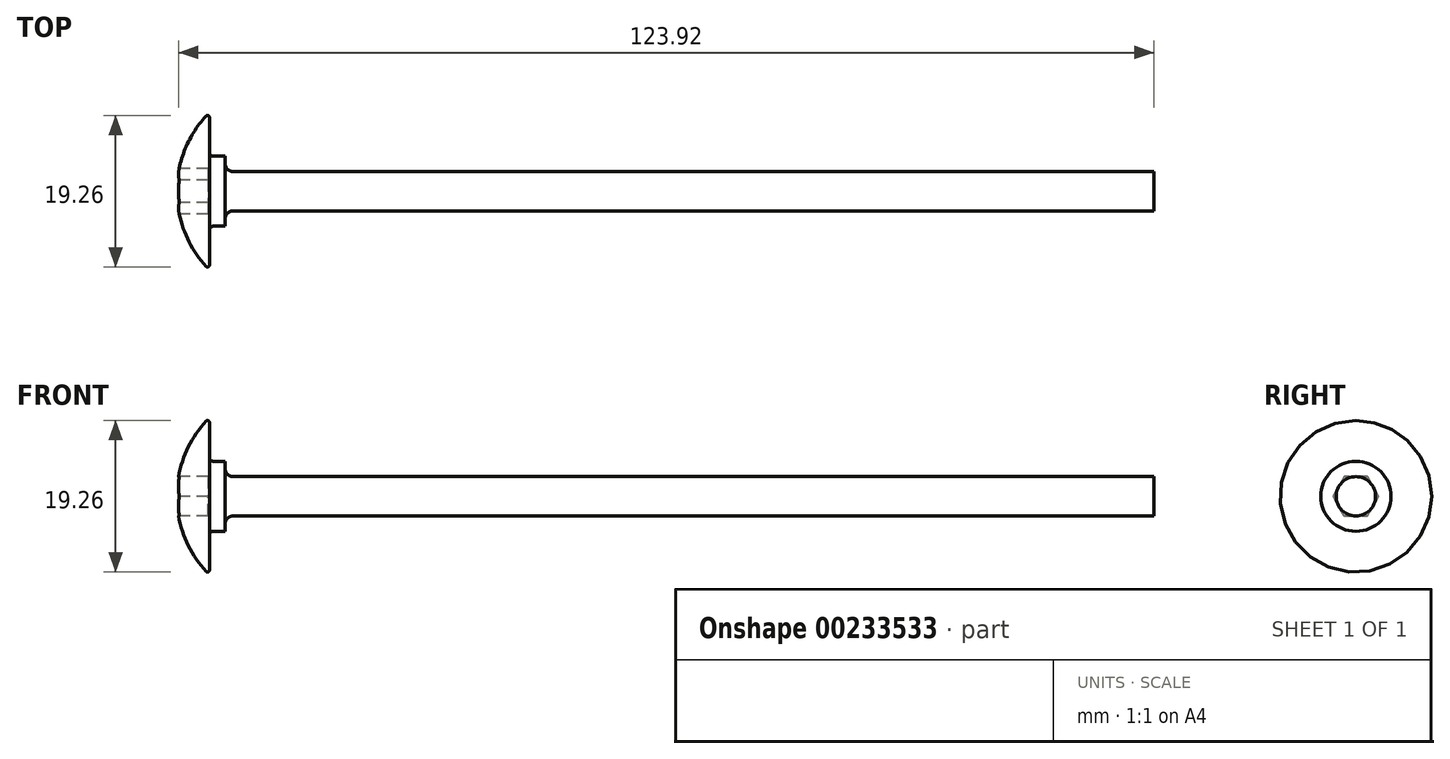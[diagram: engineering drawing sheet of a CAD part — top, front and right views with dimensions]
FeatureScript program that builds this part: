
annotation { "Feature Type Name" : "Feature", "Feature Type Description" : "" }
export const myFeature = defineFeature(function(context is Context, id is Id, definition is map)
    precondition{}
    {
        {
            var Q0;
            Q0=qCreatedBy(makeId("Top.planeOp"),FACE);
            var sketch = newSketch(context, id + "F0", { "sketchPlane" : qUnion([Q0])});
            skLineSegment(sketch, "E0", {"start": v(-82.6, 0) * mm, "end": v(124.14, 0) * mm, "construction": true});
            skLineSegment(sketch, "E1", {"start": v(124.14, 0) * mm, "end": v(124.14, 2.5) * mm});
            skLineSegment(sketch, "E2", {"start": v(124.14, 2.5) * mm, "end": v(6.14, 2.5) * mm});
            skLineSegment(sketch, "E3", {"start": v(4.14, 4.45) * mm, "end": v(4.14, 10) * mm});
            skLineSegment(sketch, "E4", {"start": v(4.14, 10) * mm, "end": v(16.1, 21.96) * mm, "construction": true});
            skLineSegment(sketch, "E5", {"start": v(0, 0) * mm, "end": v(0, -9.73) * mm, "construction": true});
            skArc(sketch, "E6", {"start": v(0, 0) * mm, "mid": v(1.08, 5.41) * mm, "end": v(4.14, 10) * mm});
            skLineSegment(sketch, "E7", {"start": v(4.14, 4.45) * mm, "end": v(6.14, 4.45) * mm});
            skLineSegment(sketch, "E8", {"start": v(6.14, 4.45) * mm, "end": v(6.14, 2.5) * mm});
            skPoint(sketch, "E9.orphan", {"position": v(4.14, 2.5) * mm});
            skLineSegment(sketch, "E10", {"start": v(0, 0) * mm, "end": v(124.14, 0) * mm});
            skSolve(sketch);
        }
        {
            var Q0;
            Q0 = qSketchRegion(id + "F0", true);
            var Q1;
            Q1=sQuery(id+"F0.wireOp",EDGE,"E0");
            revolve(context, id + "F1", {"entities" : qUnion([Q0]), "axis" : qUnion([Q1]), "revolveType" : RevolveType.FULL});
        }
        {
            var Q0;
            Q0=makeQuery(id+"F1.opRevolve","SWEPT_EDGE",EDGE,{"disambiguationData":[OSD([sQuery(id+"F0.wireOp",EDGE,"E3"),sQuery(id+"F0.wireOp",EDGE,"E6")])]});
            fillet(context, id + "F2", {"entities" : qUnion([Q0]), "radius" : 0.25 * mm, "tangentPropagation" : true, "allowEdgeOverflow" : false});
        }
        {
            var Q0;
            Q0=makeQuery(id+"F1.opRevolve","SWEPT_EDGE",EDGE,{"disambiguationData":[OSD([sQuery(id+"F0.wireOp",EDGE,"E3"),sQuery(id+"F0.wireOp",EDGE,"E7")])]});
            fillet(context, id + "F3", {"entities" : qUnion([Q0]), "radius" : 0.5 * mm, "tangentPropagation" : true, "allowEdgeOverflow" : false});
        }
        {
            var Q0;
            Q0=makeQuery(id+"F1.opRevolve","SWEPT_EDGE",EDGE,{"disambiguationData":[OSD([sQuery(id+"F0.wireOp",EDGE,"E2"),sQuery(id+"F0.wireOp",EDGE,"E8")])]});
            fillet(context, id + "F4", {"entities" : qUnion([Q0]), "radius" : 1 * mm, "tangentPropagation" : true, "allowEdgeOverflow" : false});
        }
        {
            var Q0;
            Q0=qCreatedBy(makeId("Right.planeOp"),FACE);
            var sketch = newSketch(context, id + "F5", { "sketchPlane" : qUnion([Q0])});
            skCircle(sketch, "E11.cCircle", {"center": v(0, 0) * mm, "radius": 2.5 * mm, "construction": true});
            skLineSegment(sketch, "E11.0", {"start": v(-1.44, -2.5) * mm, "end": v(-2.89, 0) * mm});
            skLineSegment(sketch, "E11.1", {"start": v(-2.89, 0) * mm, "end": v(-1.44, 2.5) * mm});
            skLineSegment(sketch, "E11.2", {"start": v(-1.44, 2.5) * mm, "end": v(1.44, 2.5) * mm});
            skLineSegment(sketch, "E11.3", {"start": v(1.44, 2.5) * mm, "end": v(2.89, 0) * mm});
            skLineSegment(sketch, "E11.4", {"start": v(2.89, 0) * mm, "end": v(1.44, -2.5) * mm});
            skLineSegment(sketch, "E11.5", {"start": v(1.44, -2.5) * mm, "end": v(-1.44, -2.5) * mm});
            skPoint(sketch, "E11.0.midPoint", {"position": v(-2.17, -1.25) * mm});
            skLineSegment(sketch, "E12", {"start": v(13.73, 0) * mm, "end": v(-17.19, 0) * mm, "construction": true});
            skLineSegment(sketch, "E13", {"start": v(0, 17.1) * mm, "end": v(0, -13.72) * mm, "construction": true});
            skSolve(sketch);
        }
        {
            var Q0;
            Q0 = qSketchRegion(id + "F5", true);
            extrude(context, id + "F6", {"entities" : qUnion([Q0]), "operationType" : NewBodyOperationType.REMOVE, "depth" : 4 * mm});
        }
    });
